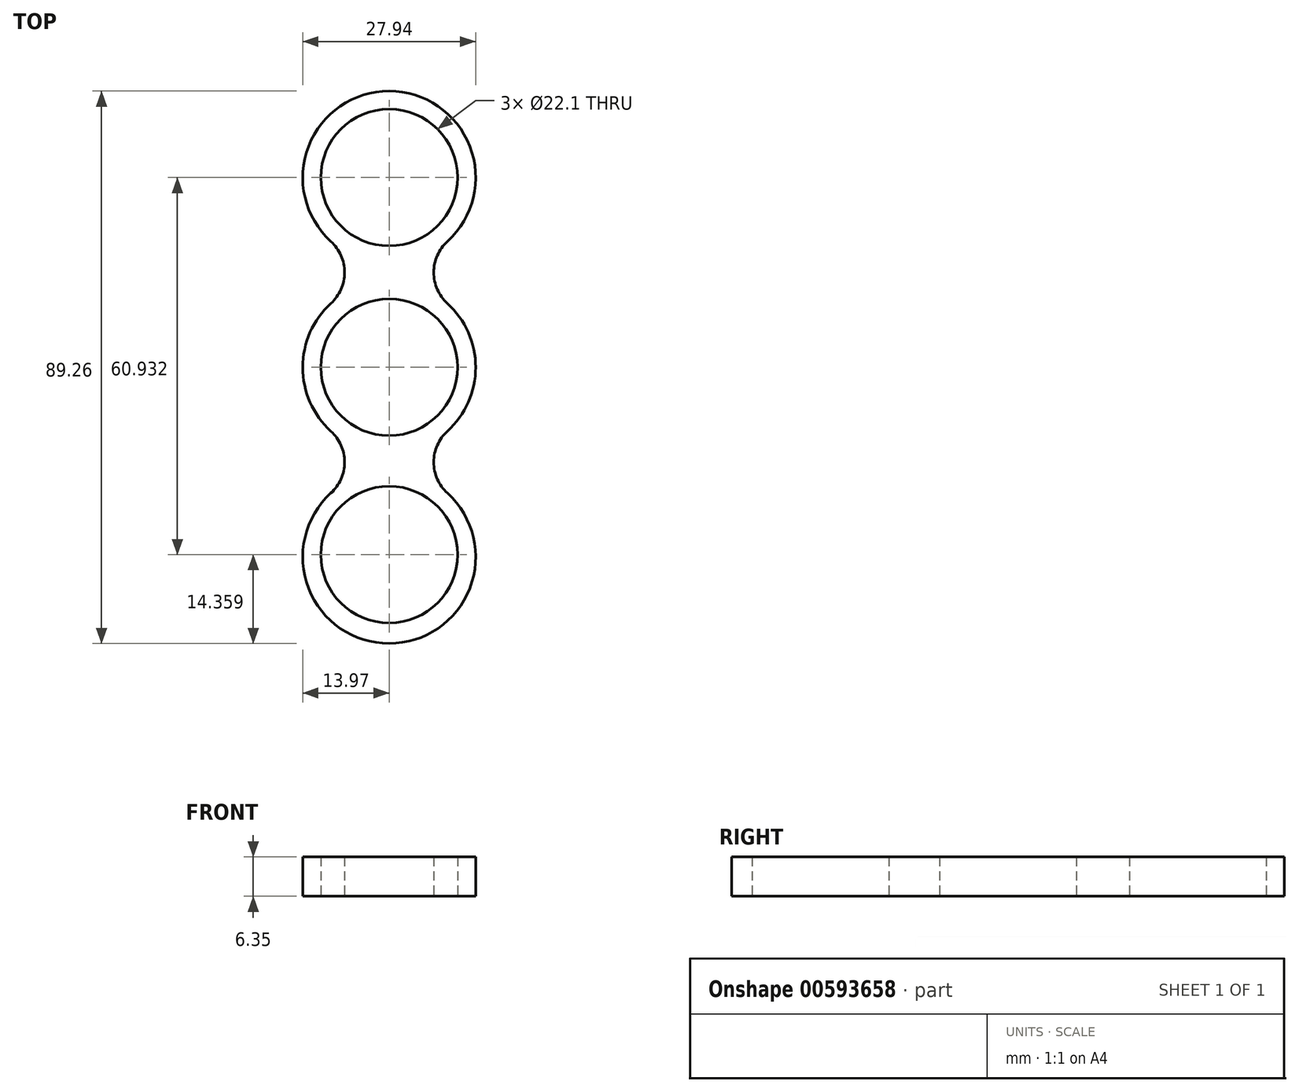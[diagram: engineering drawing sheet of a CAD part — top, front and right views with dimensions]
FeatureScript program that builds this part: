
annotation { "Feature Type Name" : "Feature", "Feature Type Description" : "" }
export const myFeature = defineFeature(function(context is Context, id is Id, definition is map)
    precondition{}
    {
        {
            var Q0;
            Q0=qCreatedBy(makeId("Top.planeOp"),FACE);
            var sketch = newSketch(context, id + "F0", { "sketchPlane" : qUnion([Q0])});
            skCircle(sketch, "E0", {"center": v(0, 0) * mm, "radius": 11.05 * mm});
            skSolve(sketch);
        }
        {
            var Q0;
            Q0=qCreatedBy(makeId("Top.planeOp"),FACE);
            var sketch = newSketch(context, id + "F1", { "sketchPlane" : qUnion([Q0])});
            skCircle(sketch, "E1", {"center": v(0, 0) * mm, "radius": 13.97 * mm});
            skSolve(sketch);
        }
        {
            var Q0;
            Q0=qCreatedBy(makeId("Top.planeOp"),FACE);
            var sketch = newSketch(context, id + "F2", { "sketchPlane" : qUnion([Q0])});
            skCircle(sketch, "E2", {"center": v(0, 30.66) * mm, "radius": 11.05 * mm});
            skCircle(sketch, "E3", {"center": v(0, 30.66) * mm, "radius": 13.97 * mm});
            skSolve(sketch);
        }
        {
            var Q0;
            Q0=qCreatedBy(makeId("Top.planeOp"),FACE);
            var sketch = newSketch(context, id + "F3", { "sketchPlane" : qUnion([Q0])});
            skCircle(sketch, "E4", {"center": v(0, -30.27) * mm, "radius": 11.05 * mm});
            skCircle(sketch, "E5", {"center": v(0, -30.27) * mm, "radius": 13.97 * mm});
            skSolve(sketch);
        }
        {
            var Q0;
            Q0=qCreatedBy(makeId("Top.planeOp"),FACE);
            var sketch = newSketch(context, id + "F4", { "sketchPlane" : qUnion([Q0])});
            skCircle(sketch, "E6.0", {"center": v(0, 30.66) * mm, "radius": 13.97 * mm});
            skCircle(sketch, "E7.0", {"center": v(0, 0) * mm, "radius": 13.97 * mm});
            skLineSegment(sketch, "E8", {"start": v(0, 0) * mm, "end": v(13.97, 0) * mm});
            skArc(sketch, "E9", {"start": v(9.4, 20.33) * mm, "mid": v(7.2, 15.33) * mm, "end": v(9.4, 10.33) * mm});
            skArc(sketch, "E10.MirrorCS", {"start": v(-9.4, 20.33) * mm, "mid": v(-7.2, 15.33) * mm, "end": v(-9.4, 10.33) * mm});
            skArc(sketch, "E11.MirrorCS", {"start": v(-9.4, -20.33) * mm, "mid": v(-7.2, -15.33) * mm, "end": v(-9.4, -10.33) * mm});
            skArc(sketch, "E12.MirrorCS", {"start": v(9.4, -20.33) * mm, "mid": v(7.2, -15.33) * mm, "end": v(9.4, -10.33) * mm});
            skCircle(sketch, "E13.MirrorC", {"center": v(0, -30.66) * mm, "radius": 13.97 * mm});
            skPoint(sketch, "E14.end.orphan", {"position": v(13.97, 30.66) * mm});
            skCircle(sketch, "E15.0", {"center": v(0, 30.66) * mm, "radius": 11.05 * mm});
            skCircle(sketch, "E16.0", {"center": v(0, 0) * mm, "radius": 11.05 * mm});
            skCircle(sketch, "E17.0.0", {"center": v(0, -30.27) * mm, "radius": 11.05 * mm});
            skSolve(sketch);
        }
        {
            var Q0;
            Q0 = qSketchRegion(id + "F4", true);
            extrude(context, id + "F5", {"entities" : qUnion([Q0]), "depth" : 6.35 * mm, "offsetDistance" : 25.4 * mm});
        }
    });
